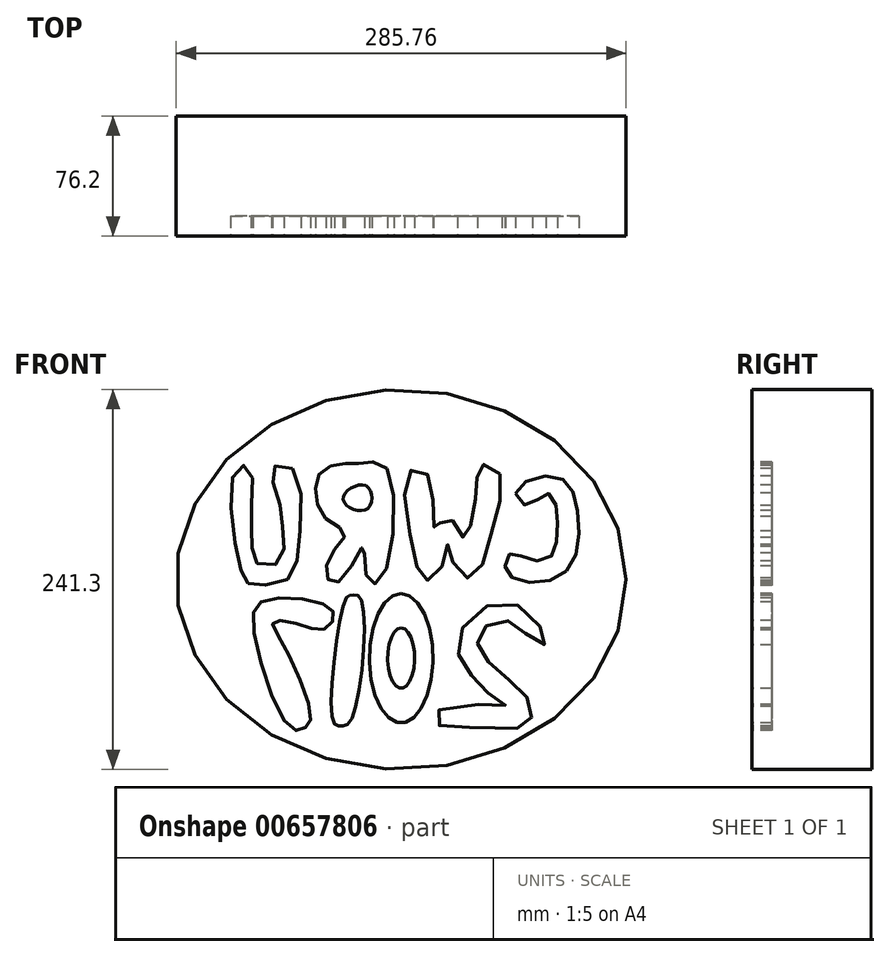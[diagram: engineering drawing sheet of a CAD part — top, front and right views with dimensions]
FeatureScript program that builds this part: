
annotation { "Feature Type Name" : "Feature", "Feature Type Description" : "" }
export const myFeature = defineFeature(function(context is Context, id is Id, definition is map)
    precondition{}
    {
        {
            var Q0;
            Q0=qCreatedBy(makeId("Front.planeOp"),FACE);
            var sketch = newSketch(context, id + "F0", { "sketchPlane" : qUnion([Q0])});
            skEllipse(sketch, "E0", {"center": v(0, 0) * mm, "majorRadius": 142.88 * mm, "minorRadius": 120.65 * mm, "majorAxis": v(1, 0)});
            skSolve(sketch);
        }
        {
            var Q0;
            Q0 = qSketchRegion(id + "F0", true);
            extrude(context, id + "F1", {"entities" : qUnion([Q0]), "depth" : 76.2 * mm, "offsetDistance" : 25.4 * mm});
        }
        {
            var Q0;
            Q0=makeQuery(id+"F1.opExtrude","CAP_FACE",FACE,{"disambiguationData":[OSD([sQuery(id+"F0.wireOp",EDGE,"E0")])],"isStart":false});
            var sketch = newSketch(context, id + "F2", { "sketchPlane" : qUnion([Q0])});
            skFitSpline(sketch, "E1", {"points": [v(72.66, 54.75) * mm, v(87.09, 65.11) * mm, v(105.22, 61.78) * mm, v(111.88, 43.65) * mm, v(110.77, 15.16) * mm, v(96.7, 0) * mm, v(73.4, 0) * mm, v(66, 7.76) * mm, v(69.7, 16.64) * mm, v(80.06, 12.94) * mm, v(95.23, 14.42) * mm, v(98.93, 28.85) * mm, v(97.82, 48.83) * mm, v(91.9, 54.75) * mm, v(81.17, 46.98) * mm, v(72.66, 54.75) * mm]});
            skFitSpline(sketch, "E2", {"points": [v(62.67, 66.96) * mm, v(58.23, 32.55) * mm, v(47.13, 2.95) * mm, v(36.03, 4.06) * mm, v(29.74, 22.2) * mm, v(24.2, 4.43) * mm, v(14.57, 0) * mm, v(6.8, 22.93) * mm, v(4.58, 67.7) * mm, v(15.31, 68.44) * mm, v(20.5, 42.54) * mm, v(21.97, 31.07) * mm, v(27.9, 39.95) * mm, v(37.14, 30.33) * mm, v(40.47, 26.63) * mm, v(46.39, 44.76) * mm, v(48.24, 64.74) * mm, v(51.57, 72.88) * mm, v(62.67, 66.96) * mm]});
            skFitSpline(sketch, "E3", {"points": [v(-9.1, 70.66) * mm, v(-12.8, 0) * mm, v(-21.32, 0) * mm, v(-23.9, 21.08) * mm, v(-37.6, 0) * mm, v(-46.48, 0) * mm, v(-44.63, 15.53) * mm, v(-35.75, 29.22) * mm, v(-47.59, 38.47) * mm, v(-54.25, 54.75) * mm, v(-50.55, 68.81) * mm, v(-36.12, 73.62) * mm, v(-23.9, 74) * mm, v(-9.1, 70.66) * mm]});
            skFitSpline(sketch, "E4", {"points": [v(-22.43, 59.56) * mm, v(-21.69, 44.76) * mm, v(-36.86, 51.05) * mm, v(-22.43, 59.56) * mm]});
            skFitSpline(sketch, "E5", {"points": [v(-69.05, 70.66) * mm, v(-64.6, 24.41) * mm, v(-72.38, 0) * mm, v(-93.84, -3.34) * mm, v(-99.39, 0) * mm, v(-106.42, 30.7) * mm, v(-104.57, 70.66) * mm, v(-96.43, 70.66) * mm, v(-95.32, 44.02) * mm, v(-94.58, 23.3) * mm, v(-91.62, 10.35) * mm, v(-77.19, 11.1) * mm, v(-74.97, 29.6) * mm, v(-77.93, 51.8) * mm, v(-81.63, 70.66) * mm, v(-69.05, 70.66) * mm]});
            skFitSpline(sketch, "E6", {"points": [v(88.34, -29.67) * mm, v(66.47, -14.33) * mm, v(40.77, -28.14) * mm, v(36.55, -48.47) * mm, v(46.9, -63.43) * mm, v(59.18, -74.94) * mm, v(66.09, -80.3) * mm, v(28.5, -80.69) * mm, v(21.2, -90.66) * mm, v(42.3, -94.12) * mm, v(61.1, -94.5) * mm, v(75.3, -94.12) * mm, v(82.58, -88.36) * mm, v(81.05, -76.47) * mm, v(68, -63.43) * mm, v(53.05, -49.62) * mm, v(48.44, -38.5) * mm, v(54.96, -28.9) * mm, v(69.54, -26.6) * mm, v(80.67, -35.8) * mm, v(91.4, -41.18) * mm, v(88.34, -29.67) * mm]});
            skEllipse(sketch, "E7", {"center": v(0, -50) * mm, "majorRadius": 19.18 * mm, "minorRadius": 8.58 * mm, "majorAxis": v(0, 1)});
            skEllipse(sketch, "E8", {"center": v(0, -50) * mm, "majorRadius": 41.04 * mm, "minorRadius": 20.24 * mm, "majorAxis": v(0, 1)});
            skFitSpline(sketch, "E9", {"points": [v(-31.34, -88.36) * mm, v(-25.97, -11.26) * mm, v(-31.34, -10.1) * mm, v(-34.8, -11.64) * mm, v(-43.24, -90.28) * mm, v(-38.25, -92.96) * mm, v(-31.34, -88.36) * mm]});
            skFitSpline(sketch, "E10", {"points": [v(-49.76, -15.48) * mm, v(-87.35, -13.56) * mm, v(-93.87, -29.67) * mm, v(-70.09, -94.5) * mm, v(-60.88, -94.12) * mm, v(-57.43, -87.98) * mm, v(-73.92, -43.1) * mm, v(-81.21, -26.99) * mm, v(-65.87, -28.14) * mm, v(-48.99, -31.59) * mm, v(-42.47, -23.53) * mm, v(-49.76, -15.48) * mm]});
            skSolve(sketch);
        }
        {
            var Q0;
            Q0 = qSketchRegion(id + "F2", true);
            extrude(context, id + "F3", {"entities" : qUnion([Q0]), "operationType" : NewBodyOperationType.REMOVE, "oppositeDirection" : true, "depth" : 12.7 * mm, "offsetDistance" : 25.4 * mm});
        }
    });
